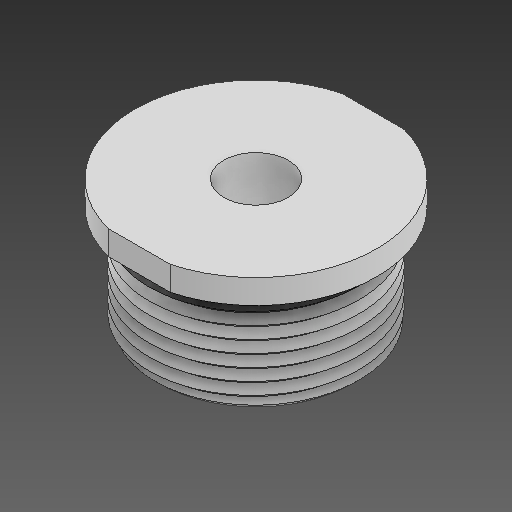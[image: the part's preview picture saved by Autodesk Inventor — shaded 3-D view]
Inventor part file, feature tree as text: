
AUTODESK INVENTOR PART (.ipt)
format: ipt  version: 2021 (Build 250183000, 183)  size: 399,872 bytes
history: native  units: in
note: dims shown in document units (in); Inventor stores cm internally (conversion verified against a paired STEP export)
features: other x3, sketch x3
ambient origin geometry x8: Origin, YZ Plane, XZ Plane, XY Plane, X Axis, Y Axis, Z Axis, Center Point
bodies: Solid1 (feature_tree)
feature tree (6):
  other  "endcap.ipt"
  other  "Solid1::endcap.ipt"
  other  "TaggingFeature1"
  sketch  "Sketch1"  dims[d0=0.3937in]
  sketch  "Sketch2"
  sketch  "Sketch3"
